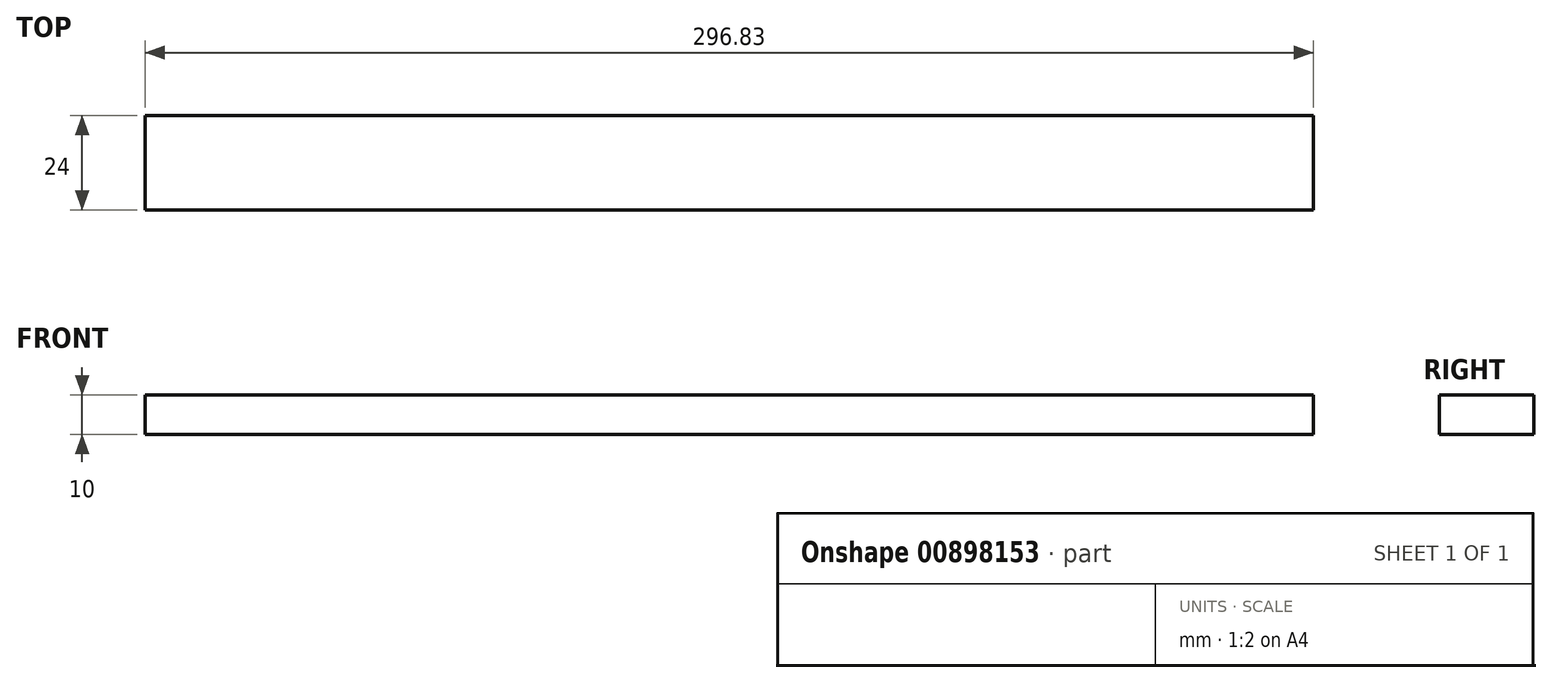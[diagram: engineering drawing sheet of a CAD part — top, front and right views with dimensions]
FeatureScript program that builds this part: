
annotation { "Feature Type Name" : "Feature", "Feature Type Description" : "" }
export const myFeature = defineFeature(function(context is Context, id is Id, definition is map)
    precondition{}
    {
        {
            var Q0;
            Q0=qCreatedBy(makeId("Top.planeOp"),FACE);
            var sketch = newSketch(context, id + "F0", { "sketchPlane" : qUnion([Q0])});
            skLineSegment(sketch, "E0.bottom", {"start": v(-154.43, 12) * mm, "end": v(142.4, 12) * mm});
            skLineSegment(sketch, "E0.top", {"start": v(-154.43, -12) * mm, "end": v(42.58, -12) * mm});
            skLineSegment(sketch, "E0.left", {"start": v(-154.43, 12) * mm, "end": v(-154.43, -12) * mm});
            skLineSegment(sketch, "E0.right", {"start": v(142.4, 12) * mm, "end": v(142.4, -12) * mm});
            skLineSegment(sketch, "E1.trimOffspring", {"start": v(42.58, -12) * mm, "end": v(142.4, -12) * mm});
            skSolve(sketch);
        }
        {
            var Q0;
            Q0=makeQuery(id+"F0.imprint","IMPRINT",FACE,{"disambiguationData":[TD([[makeQuery(id+"F0.imprint","IMPRINT",EDGE,{"derivedFrom":sQuery(id+"F0.wireOp",EDGE,"E0.bottom")}),-1.0]])]});
            extrude(context, id + "F1", {"entities" : qUnion([Q0]), "depth" : 5 * mm, "offsetDistance" : 25 * mm, "hasSecondDirection" : true, "secondDirectionOppositeDirection" : true, "secondDirectionDepth" : 5 * mm});
        }
    });
